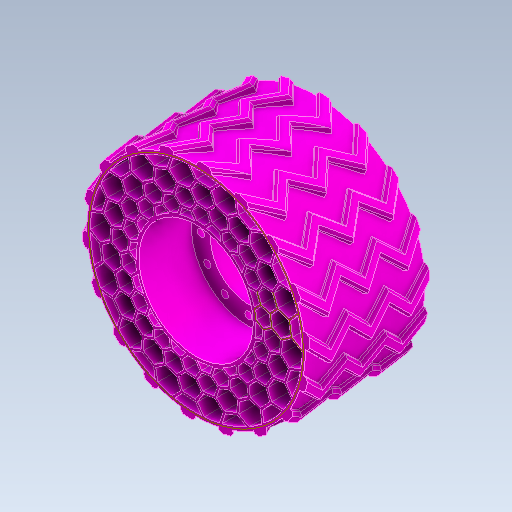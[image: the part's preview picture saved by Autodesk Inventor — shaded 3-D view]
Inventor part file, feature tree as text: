
AUTODESK INVENTOR PART (.ipt)
format: ipt  version: 2023 (Build 270158000, 158)  size: 1,652,224 bytes
history: native  units: in
note: dims shown in document units (in); Inventor stores cm internally (conversion verified against a paired STEP export)
features: other x38, sketch x5, plane x2
ambient origin geometry x8: Origin, YZ Plane, XZ Plane, XY Plane, X Axis, Y Axis, Z Axis, Center Point
bodies: Solid1 (feature_tree)
feature tree (45):
  other  "Tire_v8.ipt"
  other  "Solid1::Tire_v8.ipt"
  other  "TaggingFeature1"
  sketch  "Sketch1"  dims[d0=0.3937in]
  sketch  "Sketch2"
  sketch  "Sketch3"
  sketch  "Sketch4"
  sketch  "Sketch5"
  plane  "Work Plane1"
  plane  "Work Plane2"
  other  "Work Point1"
  other  "Srf1"
  other  "Srf2"
  other  "Srf3"
  other  "Srf4"
  other  "Srf5"
  other  "Srf6"
  other  "Srf7"
  other  "Srf8"
  other  "Srf9"
  other  "Srf10"
  other  "Srf11"
  other  "Srf12"
  other  "Srf13"
  other  "Srf14"
  other  "Srf15"
  other  "Srf16"
  other  "Srf17"
  other  "Srf1::Derived"
  other  "Srf2::Derived"
  other  "Srf3::Derived"
  other  "Srf4::Derived"
  other  "Srf5::Derived"
  other  "Srf6::Derived"
  other  "Srf7::Derived"
  other  "Srf8::Derived"
  other  "Srf9::Derived"
  other  "Srf10::Derived"
  other  "Srf11::Derived"
  other  "Srf12::Derived"
  other  "Srf13::Derived"
  other  "Srf14::Derived"
  other  "Srf15::Derived"
  other  "Srf16::Derived"
  other  "Srf17::Derived"
